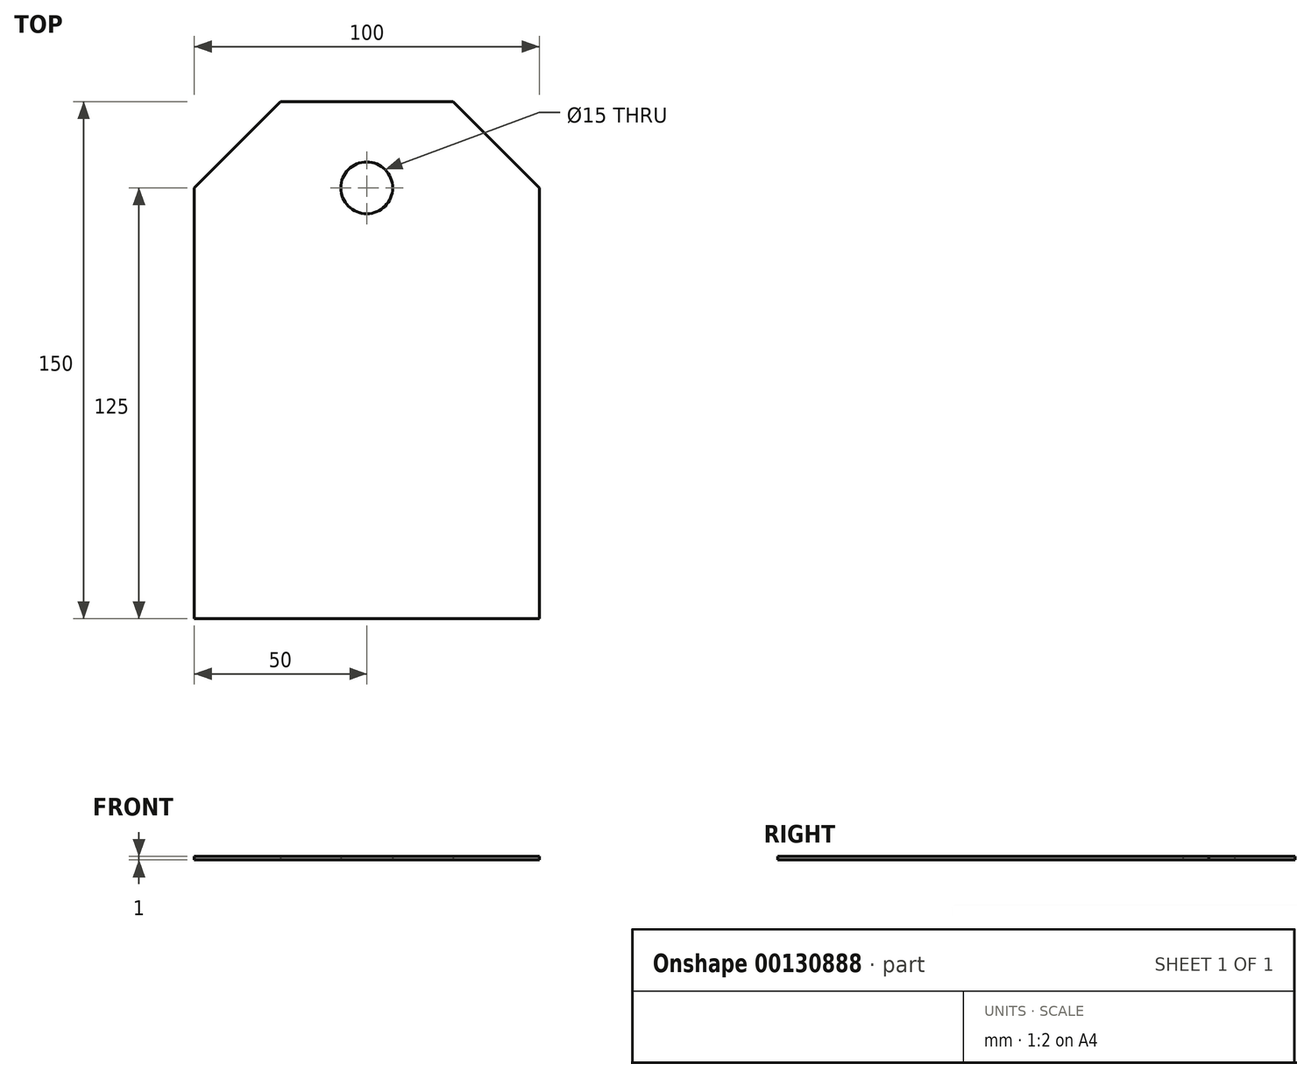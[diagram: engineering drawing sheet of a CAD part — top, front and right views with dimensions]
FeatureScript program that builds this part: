
annotation { "Feature Type Name" : "Feature", "Feature Type Description" : "" }
export const myFeature = defineFeature(function(context is Context, id is Id, definition is map)
    precondition{}
    {
        {
            var Q0;
            Q0=qCreatedBy(makeId("Top.planeOp"),FACE);
            var sketch = newSketch(context, id + "F0", { "sketchPlane" : qUnion([Q0])});
            skLineSegment(sketch, "E0.bottom", {"start": v(0, 0) * mm, "end": v(100, 0) * mm});
            skLineSegment(sketch, "E0.left", {"start": v(0, 0) * mm, "end": v(0, 125) * mm});
            skLineSegment(sketch, "E0.right", {"start": v(100, 0) * mm, "end": v(100, 125) * mm});
            skLineSegment(sketch, "E1", {"start": v(25, 150) * mm, "end": v(0, 125) * mm});
            skLineSegment(sketch, "E2", {"start": v(100, 125) * mm, "end": v(75, 150) * mm});
            skCircle(sketch, "E3", {"center": v(50, 125) * mm, "radius": 7.5 * mm});
            skLineSegment(sketch, "E4", {"start": v(25, 150) * mm, "end": v(75, 150) * mm});
            skSolve(sketch);
        }
        {
            var Q0;
            Q0 = qSketchRegion(id + "F0", true);
            var Q1;
            Q1=makeQuery(id+"F0.imprint","IMPRINT",FACE,{"disambiguationData":[TD([[makeQuery(id+"F0.imprint","IMPRINT",EDGE,{"derivedFrom":sQuery(id+"F0.wireOp",EDGE,"E0.bottom")}),1.0]])]});
            extrude(context, id + "F1", {"entities" : qUnion([Q0, Q1]), "depth" : 1 * mm});
        }
    });
